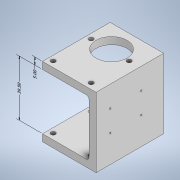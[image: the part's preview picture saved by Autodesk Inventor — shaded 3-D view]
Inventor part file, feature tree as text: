
AUTODESK INVENTOR PART (.ipt)
format: ipt  version: 2022 (Build 260153000, 153)  size: 187,904 bytes
history: native  units: mm
features: sketch x5, other x3, hole x3, extrude x2, fillet x1
ambient origin geometry x8: Origin, YZ Plane, XZ Plane, XY Plane, X Axis, Y Axis, Z Axis, Center Point
bodies: Body1 (feature_tree)
feature tree (14):
  other  "ソリッド1"
  extrude  "押し出し1"  Depth=48.0mm
  extrude  "押し出し2"  Depth=38.0mm
  hole  "穴1"  [1 undecoded]
  hole  "穴2"  [1 undecoded]
  hole  "穴4"  [1 undecoded]
  fillet  "フィレット1"  Radius=5.0mm
  sketch  "スケッチ1"
  sketch  "スケッチ2"
  sketch  "スケッチ3"
  sketch  "スケッチ4"
  sketch  "スケッチ6"
  other  "長さ寸法 1"
  other  "長さ寸法 2"
note: 3 required parameter values undecoded (feature->parameter linkage not recoverable at this tier; creation-order binding heuristic only, values carry confidence <= 0.55)
